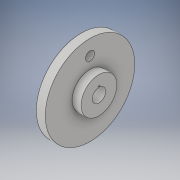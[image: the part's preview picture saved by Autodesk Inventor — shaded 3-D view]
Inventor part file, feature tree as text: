
AUTODESK INVENTOR PART (.ipt)
format: ipt  version: 2018 (Build 220112000, 112)  size: 129,536 bytes
history: native  units: in
note: dims shown in document units (in); Inventor stores cm internally (conversion verified against a paired STEP export)
features: sketch x3, revolve x1, extrude x1, hole x1
ambient origin geometry x8: Origin, YZ Plane, XZ Plane, XY Plane, X Axis, Y Axis, Z Axis, Center Point
bodies: Solid1 (feature_tree)
feature tree (6):
  revolve  "Revolution1"  [1 undecoded]
  extrude  "Extrusion1"  Depth=1.0in
  hole  "Hole1"  [1 undecoded]
  sketch  "Sketch1"  dims[d0=0.5in d1=2.125in]
  sketch  "Sketch3"  dims[d4=1.0in d5=0.625in]
  sketch  "Sketch4"  dims[d6=0.375in d7=90.0deg d9=0.05in d10=0.05in d11=1.0in d12=0.0in d13=1.65in d14=0.5in d15=0.75in d16=0.375in d17=0.25in d18=0.5635in d19=1.0in d20=0.8108in]
note: 2 required parameter values undecoded (feature->parameter linkage not recoverable at this tier; creation-order binding heuristic only, values carry confidence <= 0.55)